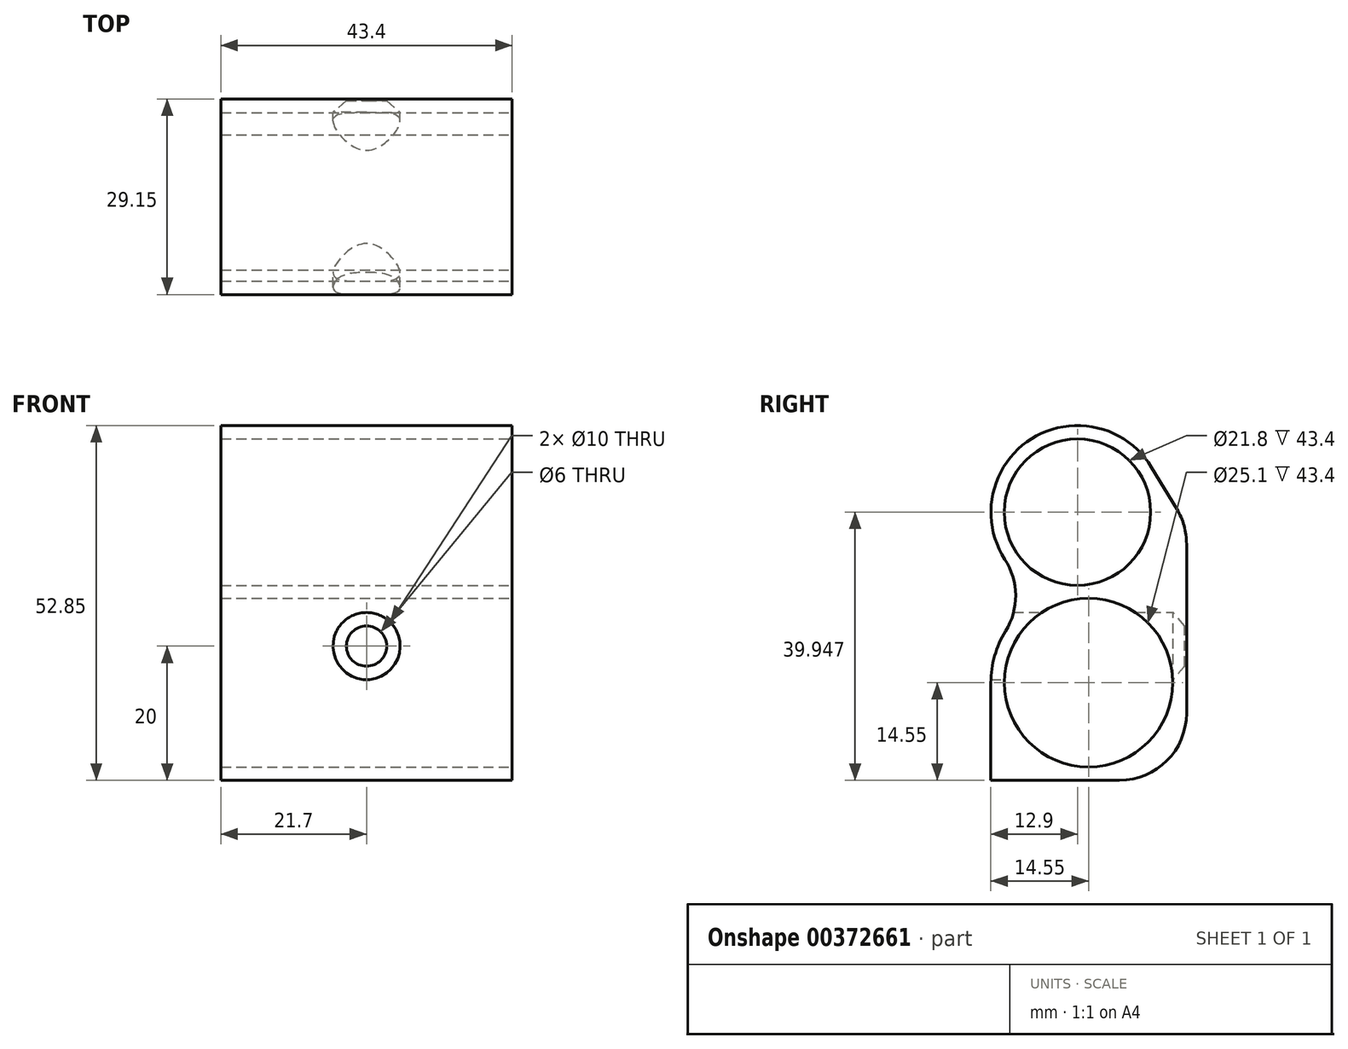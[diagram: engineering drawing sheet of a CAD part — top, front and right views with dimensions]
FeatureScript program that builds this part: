
annotation { "Feature Type Name" : "Feature", "Feature Type Description" : "" }
export const myFeature = defineFeature(function(context is Context, id is Id, definition is map)
    precondition{}
    {
        {
            var Q0;
            Q0=qCreatedBy(makeId("Front.planeOp"),FACE);
            var sketch = newSketch(context, id + "F0", { "sketchPlane" : qUnion([Q0])});
            skLineSegment(sketch, "E0.bottom", {"start": v(21.7, -20) * mm, "end": v(-21.7, -20) * mm});
            skLineSegment(sketch, "E0.top", {"start": v(21.7, 18) * mm, "end": v(-21.7, 18) * mm});
            skLineSegment(sketch, "E0.left", {"start": v(21.7, -20) * mm, "end": v(21.7, 18) * mm});
            skLineSegment(sketch, "E0.right", {"start": v(-21.7, -20) * mm, "end": v(-21.7, 18) * mm});
            skCircle(sketch, "E1", {"center": v(0, 0) * mm, "radius": 3 * mm});
            skSolve(sketch);
        }
        {
            var Q0;
            Q0=makeQuery(id+"F0.imprint","IMPRINT",FACE,{"disambiguationData":[TD([[makeQuery(id+"F0.imprint","IMPRINT",EDGE,{"derivedFrom":sQuery(id+"F0.wireOp",EDGE,"E0.left")}),-1.0]])]});
            var Q1;
            Q1=makeQuery(id+"F0.imprint","IMPRINT",FACE,{"disambiguationData":[TD([[makeQuery(id+"F0.imprint","IMPRINT",EDGE,{"derivedFrom":sQuery(id+"F0.wireOp",EDGE,"E0.bottom")}),-1.0]])]});
            var Q2;
            Q2=makeQuery(id+"F0.imprint","IMPRINT",FACE,{"disambiguationData":[TD([[makeQuery(id+"F0.imprint","IMPRINT",EDGE,{"derivedFrom":sQuery(id+"F0.wireOp",EDGE,"E0.right")}),1.0]])]});
            extrude(context, id + "F1", {"entities" : qUnion([Q0, Q1, Q2]), "depth" : 2 * mm, "offsetDistance" : 25 * mm});
        }
        {
            var Q0;
            Q0=qCreatedBy(makeId("Right.planeOp"),FACE);
            var sketch = newSketch(context, id + "F2", { "sketchPlane" : qUnion([Q0])});
            skCircle(sketch, "E2", {"center": v(-14.6, -5.45) * mm, "radius": 12.55 * mm});
            skArc(sketch, "E3", {"start": v(-26.97, 2.22) * mm, "mid": v(-28.6, -1.46) * mm, "end": v(-29.15, -5.45) * mm});
            skCircle(sketch, "E4", {"center": v(-16.25, 19.95) * mm, "radius": 10.9 * mm});
            skArc(sketch, "E5", {"start": v(-5.21, 26.62) * mm, "mid": v(-23.1, 30.88) * mm, "end": v(-27.07, 12.93) * mm});
            skPoint(sketch, "E6.visualSharp", {"position": v(-20.6, 7.8) * mm});
            skArc(sketch, "E6.filletArc", {"start": v(-26.97, 2.22) * mm, "mid": v(-25.46, 7.59) * mm, "end": v(-27.07, 12.93) * mm});
            skLineSegment(sketch, "E7", {"start": v(-27.15, -5.45) * mm, "end": v(-27.15, 19.95) * mm, "construction": true});
            skLineSegment(sketch, "E8", {"start": v(-5.21, 26.62) * mm, "end": v(0, 18) * mm});
            skLineSegment(sketch, "E9", {"start": v(-29.15, -20) * mm, "end": v(-2, -20) * mm});
            skLineSegment(sketch, "E10", {"start": v(-29.15, -5.45) * mm, "end": v(-29.15, -20) * mm});
            skLineSegment(sketch, "E11", {"start": v(-2, 18) * mm, "end": v(-2, -20) * mm});
            skLineSegment(sketch, "E12", {"start": v(-2, 18) * mm, "end": v(0, 18) * mm});
            skSolve(sketch);
        }
        {
            var Q0;
            Q0=makeQuery(id+"F2.imprint","IMPRINT",FACE,{"disambiguationData":[TD([[makeQuery(id+"F2.imprint","IMPRINT",EDGE,{"derivedFrom":sQuery(id+"F2.wireOp",EDGE,"E2")}),-1.0]])]});
            var Q1;
            Q1=makeQuery(id+"F1.opExtrude","SWEPT_FACE",FACE,{"disambiguationData":[OSD([sQuery(id+"F0.wireOp",EDGE,"E0.right")])]});
            var Q2;
            Q2=makeQuery(id+"F1.opExtrude","SWEPT_FACE",FACE,{"disambiguationData":[OSD([sQuery(id+"F0.wireOp",EDGE,"E0.left")])]});
            extrude(context, id + "F3", {"entities" : qUnion([Q0]), "operationType" : NewBodyOperationType.ADD, "endBound" : BoundingType.UP_TO_SURFACE, "oppositeDirection" : true, "depth" : 25 * mm, "endBoundEntityFace" : qUnion([Q1]), "offsetDistance" : 10 * mm, "hasSecondDirection" : true, "secondDirectionBound" : BoundingType.UP_TO_SURFACE, "secondDirectionOppositeDirection" : false, "secondDirectionDepth" : 25 * mm, "secondDirectionBoundEntityFace" : qUnion([Q2])});
        }
        {
            var Q0;
            Q0=makeQuery(id+"F3.opExtrude","SWEPT_FACE",FACE,{"disambiguationData":[OSD([sQuery(id+"F2.wireOp",EDGE,"E11")])]});
            var sketch = newSketch(context, id + "F4", { "sketchPlane" : qUnion([Q0])});
            skCircle(sketch, "E13", {"center": v(0, 0) * mm, "radius": 5 * mm});
            skSolve(sketch);
        }
        {
            var Q0;
            Q0=qSketchRegion(id+"F4",true);
            extrude(context, id + "F5", {"entities" : qUnion([Q0]), "operationType" : NewBodyOperationType.REMOVE, "endBound" : BoundingType.THROUGH_ALL, "oppositeDirection" : true, "depth" : 25 * mm, "offsetDistance" : 25 * mm});
        }
        {
            var Q0;
            Q0=qCreatedBy(makeId("Top.planeOp"),FACE);
            var sketch = newSketch(context, id + "F6", { "sketchPlane" : qUnion([Q0])});
            skLineSegment(sketch, "E14", {"start": v(0, 0) * mm, "end": v(0, -2) * mm});
            skLineSegment(sketch, "E15", {"start": v(0, -2) * mm, "end": v(-5, -2) * mm});
            skLineSegment(sketch, "E16", {"start": v(-5, -2) * mm, "end": v(-3, -0.3) * mm});
            skLineSegment(sketch, "E17", {"start": v(-3, -0.3) * mm, "end": v(-3, 0) * mm});
            skLineSegment(sketch, "E18", {"start": v(-3, 0) * mm, "end": v(0, 0) * mm});
            skSolve(sketch);
        }
        {
            var Q0;
            Q0=qSketchRegion(id+"F6",true);
            var Q1;
            Q1=sQuery(id+"F6.wireOp",EDGE,"E14");
            revolve(context, id + "F7", {"operationType" : NewBodyOperationType.REMOVE, "surfaceOperationType" : NewSurfaceOperationType.NEW, "entities" : qUnion([Q0]), "axis" : qUnion([Q1]), "revolveType" : RevolveType.FULL, "oppositeDirection" : true});
        }
        {
            var Q0;
            Q0=makeQuery(id+"F1.opExtrude","CAP_EDGE",EDGE,{"disambiguationData":[OSD([sQuery(id+"F0.wireOp",EDGE,"E0.bottom"),sQuery(id+"F0.wireOp",EDGE,"ZMjIRZOt-w7J3-Gx4m-IBQk-1eEX7ltgSaOL"),sQuery(id+"F0.wireOp",EDGE,"6qsIwgVi-Q5wO-p2fB-fZag-2frHfxhiyAUB")])],"isStart":true});
            var Q1;
            Q1=makeQuery(id+"F3.boolean.opBoolean","MERGE",EDGE,{"derivedFrom":[makeQuery(id+"F1.opExtrude","CAP_EDGE",EDGE,{"disambiguationData":[OSD([sQuery(id+"F0.wireOp",EDGE,"E0.top")])],"isStart":true}),makeQuery(id+"F3.opExtrude","TWEAK_EDGE",EDGE,{"derivedFrom":[makeQuery(id+"F2.imprint","IMPRINT",EDGE,{"derivedFrom":sQuery(id+"F2.wireOp",EDGE,"E8")}),makeQuery(id+"F2.imprint","IMPRINT",EDGE,{"derivedFrom":sQuery(id+"F2.wireOp",EDGE,"E12")})]})]});
            var Q2;
            Q2=makeQuery(id+"F3.opExtrude","TWEAK_EDGE",EDGE,{"derivedFrom":[makeQuery(id+"F2.imprint","IMPRINT",EDGE,{"derivedFrom":sQuery(id+"F2.wireOp",EDGE,"E9")}),makeQuery(id+"F2.imprint","IMPRINT",EDGE,{"derivedFrom":sQuery(id+"F2.wireOp",EDGE,"E10")})]});
            fillet(context, id + "F8", {"entities" : qUnion([Q0, Q1, Q2]), "radius" : 10 * mm, "tangentPropagation" : true, "allowEdgeOverflow" : false});
        }
    });
